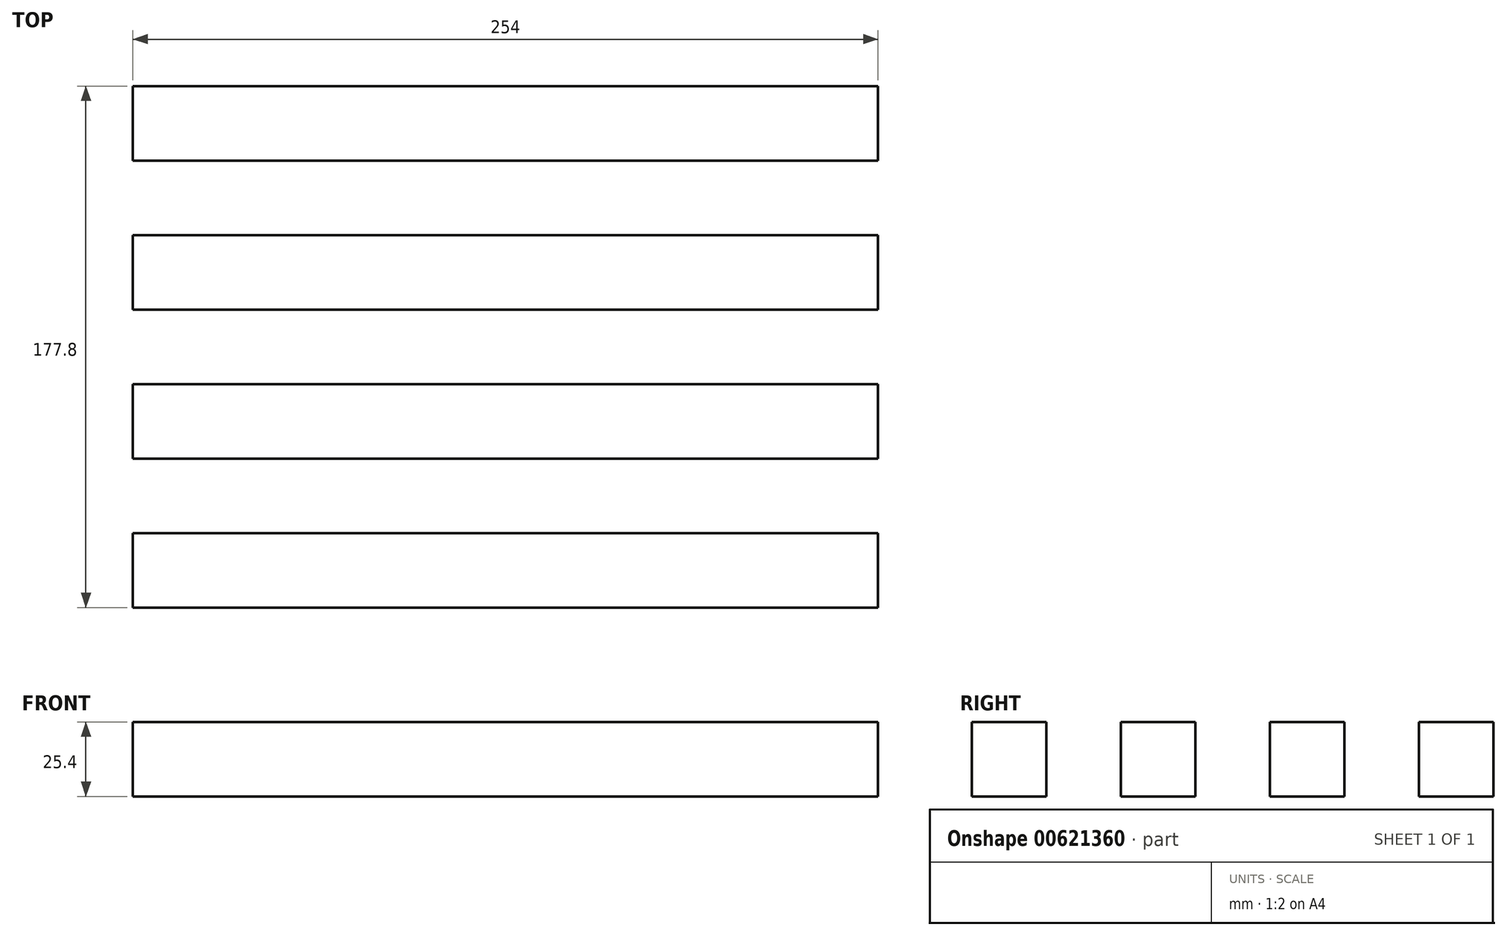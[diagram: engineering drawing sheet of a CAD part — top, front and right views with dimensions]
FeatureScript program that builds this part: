
annotation { "Feature Type Name" : "Feature", "Feature Type Description" : "" }
export const myFeature = defineFeature(function(context is Context, id is Id, definition is map)
    precondition{}
    {
        {
            var Q0;
            Q0=qCreatedBy(makeId("Top.planeOp"),FACE);
            var sketch = newSketch(context, id + "F0", { "sketchPlane" : qUnion([Q0])});
            skLineSegment(sketch, "E0", {"start": v(0.21, 0.12) * mm, "end": v(25.61, 0.12) * mm});
            skLineSegment(sketch, "E1", {"start": v(25.61, 0.12) * mm, "end": v(51.01, 0.12) * mm});
            skLineSegment(sketch, "E2", {"start": v(51.01, 0.12) * mm, "end": v(76.41, 0.12) * mm});
            skLineSegment(sketch, "E3", {"start": v(76.41, 0.12) * mm, "end": v(101.81, 0.12) * mm});
            skLineSegment(sketch, "E4", {"start": v(101.81, 0.12) * mm, "end": v(127.21, 0.12) * mm});
            skLineSegment(sketch, "E5", {"start": v(127.21, 0.12) * mm, "end": v(152.61, 0.12) * mm});
            skPoint(sketch, "E5.endSnap0", {"position": v(114.51, 0.12) * mm});
            skLineSegment(sketch, "E6", {"start": v(152.61, 0.12) * mm, "end": v(178.01, 0.12) * mm});
            skLineSegment(sketch, "E7", {"start": v(178.01, 0.12) * mm, "end": v(203.41, 0.12) * mm});
            skLineSegment(sketch, "E8", {"start": v(203.41, 0.12) * mm, "end": v(228.81, 0.12) * mm});
            skLineSegment(sketch, "E9", {"start": v(228.81, 0.12) * mm, "end": v(254.21, 0.12) * mm});
            skLineSegment(sketch, "E10", {"start": v(254.21, 0.12) * mm, "end": v(254.21, 25.52) * mm});
            skLineSegment(sketch, "E11", {"start": v(254.21, 25.52) * mm, "end": v(254.21, 50.92) * mm});
            skLineSegment(sketch, "E12", {"start": v(254.21, 50.92) * mm, "end": v(254.21, 76.32) * mm});
            skLineSegment(sketch, "E13", {"start": v(254.21, 76.32) * mm, "end": v(254.21, 101.72) * mm});
            skLineSegment(sketch, "E14", {"start": v(254.21, 101.72) * mm, "end": v(254.21, 127.12) * mm});
            skLineSegment(sketch, "E15", {"start": v(254.21, 127.12) * mm, "end": v(254.21, 152.52) * mm});
            skLineSegment(sketch, "E16", {"start": v(254.21, 152.52) * mm, "end": v(254.21, 177.92) * mm});
            skLineSegment(sketch, "E17", {"start": v(254.21, 177.92) * mm, "end": v(254.21, 203.32) * mm});
            skLineSegment(sketch, "E18", {"start": v(254.21, 203.32) * mm, "end": v(0.21, 203.32) * mm});
            skLineSegment(sketch, "E19", {"start": v(0.21, 203.32) * mm, "end": v(0.21, 0.12) * mm});
            skLineSegment(sketch, "E20", {"start": v(254.21, 76.32) * mm, "end": v(0.21, 76.32) * mm});
            skLineSegment(sketch, "E21", {"start": v(254.21, 101.72) * mm, "end": v(0, 101.72) * mm});
            skLineSegment(sketch, "E22", {"start": v(254.21, 177.92) * mm, "end": v(0, 177.92) * mm});
            skLineSegment(sketch, "E23", {"start": v(254.21, 152.52) * mm, "end": v(0.21, 152.52) * mm});
            skLineSegment(sketch, "E24", {"start": v(254.21, 127.12) * mm, "end": v(0, 127.12) * mm});
            skLineSegment(sketch, "E25", {"start": v(254.21, 50.92) * mm, "end": v(0, 50.92) * mm});
            skLineSegment(sketch, "E26", {"start": v(254.21, 25.52) * mm, "end": v(0, 25.52) * mm});
            skSolve(sketch);
        }
        {
            var Q0;
            {var subQ0=sQuery(id+"F0.wireOp",EDGE,"E0");Q0=makeQuery(id+"F0.imprint","IMPRINT",FACE,{"disambiguationData":[TD([[makeQuery(id+"F0.imprint","IMPRINT",EDGE,{"derivedFrom":subQ0}),1.0]])]});}
            var Q1;
            {var subQ0=sQuery(id+"F0.wireOp",EDGE,"E12");Q1=makeQuery(id+"F0.imprint","IMPRINT",FACE,{"disambiguationData":[TD([[makeQuery(id+"F0.imprint","IMPRINT",EDGE,{"derivedFrom":subQ0}),1.0]])]});}
            var Q2;
            {var subQ0=sQuery(id+"F0.wireOp",EDGE,"E14");Q2=makeQuery(id+"F0.imprint","IMPRINT",FACE,{"disambiguationData":[TD([[makeQuery(id+"F0.imprint","IMPRINT",EDGE,{"derivedFrom":subQ0}),1.0]])]});}
            var Q3;
            {var subQ0=sQuery(id+"F0.wireOp",EDGE,"E16");Q3=makeQuery(id+"F0.imprint","IMPRINT",FACE,{"disambiguationData":[TD([[makeQuery(id+"F0.imprint","IMPRINT",EDGE,{"derivedFrom":subQ0}),1.0]])]});}
            extrude(context, id + "F1", {"entities" : qUnion([Q0, Q1, Q2, Q3]), "depth" : 25.4 * mm, "offsetDistance" : 25.4 * mm});
        }
    });
